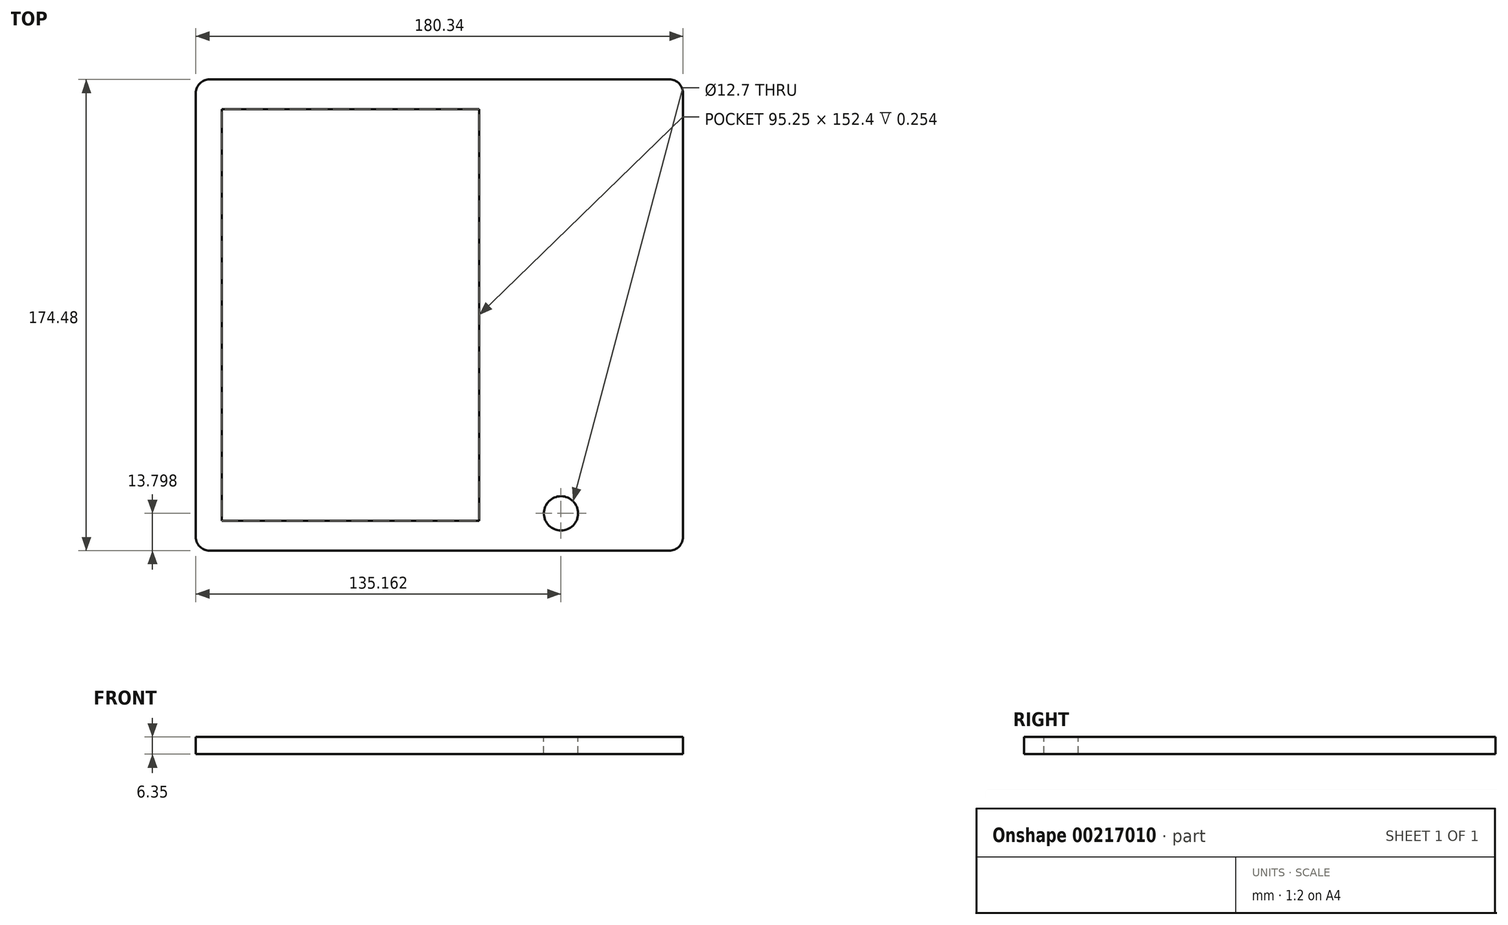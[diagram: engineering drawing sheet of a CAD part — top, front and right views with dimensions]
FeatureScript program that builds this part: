
annotation { "Feature Type Name" : "Feature", "Feature Type Description" : "" }
export const myFeature = defineFeature(function(context is Context, id is Id, definition is map)
    precondition{}
    {
        {
            var Q0;
            Q0=qCreatedBy(makeId("Top.planeOp"),FACE);
            var sketch = newSketch(context, id + "F0", { "sketchPlane" : qUnion([Q0])});
            skLineSegment(sketch, "E0.0", {"start": v(-98.04, -135.64) * mm, "end": v(-98.04, 38.84) * mm});
            skLineSegment(sketch, "E0.1", {"start": v(82.3, -135.64) * mm, "end": v(-98.04, -135.64) * mm});
            skLineSegment(sketch, "E0.2", {"start": v(82.3, -135.64) * mm, "end": v(82.3, 38.84) * mm});
            skLineSegment(sketch, "E0.3", {"start": v(82.3, 38.84) * mm, "end": v(-98.04, 38.84) * mm});
            skSolve(sketch);
        }
        {
            var Q0;
            Q0=makeQuery(id+"F0.imprint","IMPRINT",FACE,{"disambiguationData":[TD([[makeQuery(id+"F0.imprint","IMPRINT",EDGE,{"derivedFrom":sQuery(id+"F0.wireOp",EDGE,"E0.0")}),-1.0]])]});
            extrude(context, id + "F1", {"entities" : qUnion([Q0]), "depth" : 6.35 * mm});
        }
        {
            var Q0;
            Q0=makeQuery(id+"F1.opExtrude","SWEPT_EDGE",EDGE,{"disambiguationData":[OSD([sQuery(id+"F0.wireOp",EDGE,"E0.0"),sQuery(id+"F0.wireOp",EDGE,"E0.1")])]});
            var Q1;
            Q1=makeQuery(id+"F1.opExtrude","SWEPT_EDGE",EDGE,{"disambiguationData":[OSD([sQuery(id+"F0.wireOp",EDGE,"E0.1"),sQuery(id+"F0.wireOp",EDGE,"E0.2")])]});
            var Q2;
            Q2=makeQuery(id+"F1.opExtrude","SWEPT_EDGE",EDGE,{"disambiguationData":[OSD([sQuery(id+"F0.wireOp",EDGE,"E0.0"),sQuery(id+"F0.wireOp",EDGE,"E0.3")])]});
            var Q3;
            Q3=makeQuery(id+"F1.opExtrude","SWEPT_EDGE",EDGE,{"disambiguationData":[OSD([sQuery(id+"F0.wireOp",EDGE,"E0.2"),sQuery(id+"F0.wireOp",EDGE,"E0.3")])]});
            fillet(context, id + "F2", {"entities" : qUnion([Q0, Q1, Q2, Q3]), "radius" : 5.08 * mm, "tangentPropagation" : true, "allowEdgeOverflow" : false});
        }
        {
            var Q0;
            Q0=makeQuery(id+"F1.opExtrude","CAP_FACE",FACE,{"disambiguationData":[OSD([sQuery(id+"F0.wireOp",EDGE,"E0.0"),sQuery(id+"F0.wireOp",EDGE,"E0.1"),sQuery(id+"F0.wireOp",EDGE,"E0.2"),sQuery(id+"F0.wireOp",EDGE,"E0.3")])],"isStart":false});
            var sketch = newSketch(context, id + "F3", { "sketchPlane" : qUnion([Q0])});
            skLineSegment(sketch, "E1.bottom", {"start": v(6.83, 27.8) * mm, "end": v(-88.42, 27.8) * mm});
            skLineSegment(sketch, "E1.top", {"start": v(6.83, -124.6) * mm, "end": v(-88.42, -124.6) * mm});
            skLineSegment(sketch, "E1.left", {"start": v(6.83, 27.8) * mm, "end": v(6.83, -124.6) * mm});
            skLineSegment(sketch, "E1.right", {"start": v(-88.42, 27.8) * mm, "end": v(-88.42, -124.6) * mm});
            skPoint(sketch, "E1.middle", {"position": v(-40.8, -48.4) * mm});
            skPoint(sketch, "E1.middle.positionSnap0", {"position": v(-98.04, -48.4) * mm});
            skPoint(sketch, "E1.centerSnap0", {"position": v(-98.04, -48.4) * mm});
            skCircle(sketch, "E2", {"center": v(37.12, -121.84) * mm, "radius": 6.35 * mm});
            skCircle(sketch, "E3.0.1.0", {"center": v(37.12, -73.84) * mm, "radius": 6.35 * mm});
            skCircle(sketch, "E3.0.2.0", {"center": v(37.12, -25.83) * mm, "radius": 6.35 * mm});
            skCircle(sketch, "E3.0.3.0", {"center": v(37.12, 22.18) * mm, "radius": 6.35 * mm});
            skCircle(sketch, "E3.1.1.0", {"center": v(37.12, -73.84) * mm, "radius": 6.35 * mm});
            skCircle(sketch, "E3.1.2.0", {"center": v(37.12, -25.83) * mm, "radius": 6.35 * mm});
            skCircle(sketch, "E3.1.3.0", {"center": v(37.12, 22.18) * mm, "radius": 6.35 * mm});
            skCircle(sketch, "E3.2.1.0", {"center": v(37.12, -73.84) * mm, "radius": 6.35 * mm});
            skCircle(sketch, "E3.2.2.0", {"center": v(37.12, -25.83) * mm, "radius": 6.35 * mm});
            skCircle(sketch, "E3.2.3.0", {"center": v(37.12, 22.18) * mm, "radius": 6.35 * mm});
            skLineSegment(sketch, "E3.direction1", {"start": v(37.12, -121.84) * mm, "end": v(37.12, -121.84) * mm});
            skLineSegment(sketch, "E3.direction2", {"start": v(37.12, -121.84) * mm, "end": v(37.12, -73.84) * mm, "construction": true});
            skSolve(sketch);
        }
        {
            var Q0;
            Q0=makeQuery(id+"F3.imprint","IMPRINT",FACE,{"disambiguationData":[TD([[makeQuery(id+"F3.imprint","IMPRINT",EDGE,{"derivedFrom":sQuery(id+"F3.wireOp",EDGE,"E1.bottom")}),1.0]])]});
            extrude(context, id + "F4", {"entities" : qUnion([Q0]), "operationType" : NewBodyOperationType.REMOVE, "oppositeDirection" : true, "depth" : 0.25 * mm});
        }
        {
            var Q0;
            Q0=makeQuery(id+"F3.imprint","IMPRINT",FACE,{"disambiguationData":[TD([[makeQuery(id+"F3.imprint","IMPRINT",EDGE,{"derivedFrom":sQuery(id+"F3.wireOp",EDGE,"E2")}),1.0]])]});
            var Q1;
            Q1=makeQuery(id+"F3.imprint","IMPRINT",FACE,{"disambiguationData":[TD([[makeQuery(id+"F3.imprint","IMPRINT",EDGE,{"derivedFrom":sQuery(id+"F3.wireOp",EDGE,"E3.2.1.0")}),1.0]])]});
            var Q2;
            Q2=makeQuery(id+"F3.imprint","IMPRINT",FACE,{"disambiguationData":[TD([[makeQuery(id+"F3.imprint","IMPRINT",EDGE,{"derivedFrom":sQuery(id+"F3.wireOp",EDGE,"E3.2.3.0")}),1.0]])]});
            var Q3;
            Q3=makeQuery(id+"F3.imprint","IMPRINT",FACE,{"disambiguationData":[TD([[makeQuery(id+"F3.imprint","IMPRINT",EDGE,{"derivedFrom":sQuery(id+"F3.wireOp",EDGE,"E3.2.2.0")}),1.0]])]});
            extrude(context, id + "F5", {"entities" : qUnion([Q0, Q1, Q2, Q3]), "operationType" : NewBodyOperationType.REMOVE, "oppositeDirection" : true, "depth" : 25.4 * mm});
        }
    });
